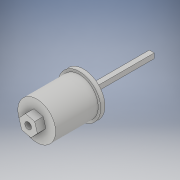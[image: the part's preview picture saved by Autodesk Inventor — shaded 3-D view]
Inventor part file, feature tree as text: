
AUTODESK INVENTOR PART (.ipt)
format: ipt  version: 2018 (Build 220112000, 112)  size: 134,656 bytes
history: native  units: in
note: dims shown in document units (in); Inventor stores cm internally (conversion verified against a paired STEP export)
features: sketch x6, extrude x5
ambient origin geometry x8: Origin, YZ Plane, XZ Plane, XY Plane, X Axis, Y Axis, Z Axis, Center Point
bodies: Solid1 (feature_tree)
feature tree (11):
  extrude  "Extrusion1"  Depth=0.125in TaperAngle=0.0deg
  extrude  "Extrusion2"  Depth=1.25in TaperAngle=0.0deg
  extrude  "Extrusion3"  Depth=0.25in TaperAngle=0.0deg
  extrude  "Extrusion4"  Depth=0.75in TaperAngle=0.0deg
  extrude  "Extrusion5"  Depth=2.0in TaperAngle=0.0deg
  sketch  "Sketch6"
  sketch  "Sketch1"  dims[d0=1.25in d1=0.125in d2=0.0in]
  sketch  "Sketch2"  dims[d3=1.105in d4=1.25in d5=0.0in]
  sketch  "Sketch3"  dims[d6=0.48in d7=0.25in d8=0.0in]
  sketch  "Sketch4"  dims[d9=0.193in d10=0.75in d11=0.0in]
  sketch  "Sketch5"  dims[d12=0.145in d13=2.0in d14=0.0in]
